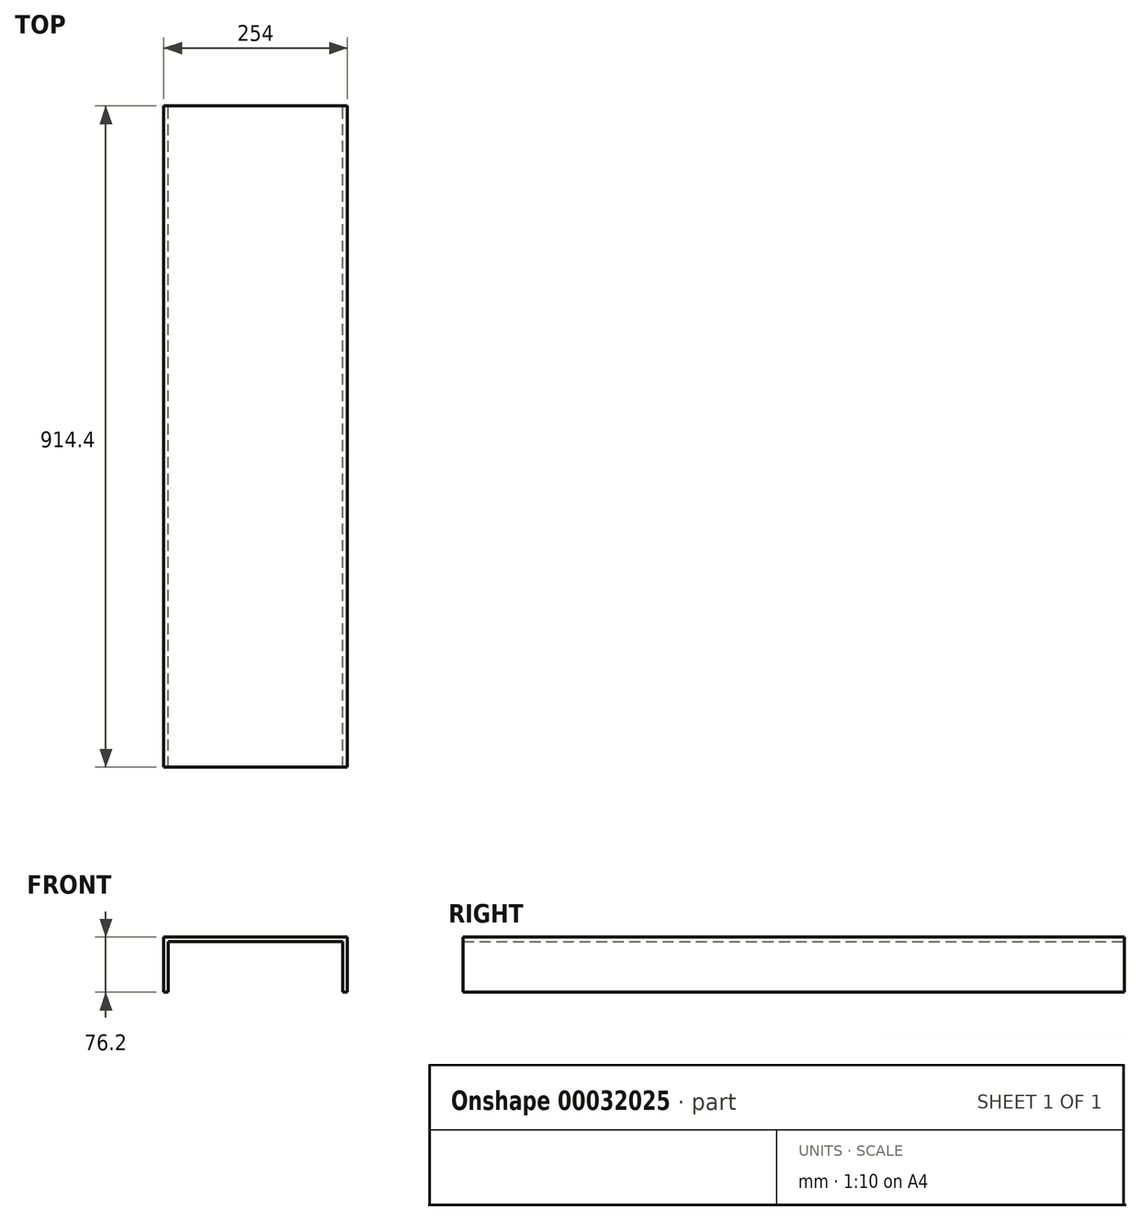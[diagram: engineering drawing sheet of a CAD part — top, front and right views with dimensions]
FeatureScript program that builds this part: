
annotation { "Feature Type Name" : "Feature", "Feature Type Description" : "" }
export const myFeature = defineFeature(function(context is Context, id is Id, definition is map)
    precondition{}
    {
        {
            var Q0;
            Q0=qCreatedBy(makeId("Front.planeOp"),FACE);
            var sketch = newSketch(context, id + "F0", { "sketchPlane" : qUnion([Q0])});
            skLineSegment(sketch, "E0.bottom", {"start": v(0, 0) * mm, "end": v(6.35, 0) * mm});
            skLineSegment(sketch, "E0.top", {"start": v(0, 76.2) * mm, "end": v(254, 76.2) * mm});
            skLineSegment(sketch, "E0.left", {"start": v(0, 0) * mm, "end": v(0, 76.2) * mm});
            skLineSegment(sketch, "E0.right", {"start": v(254, 0) * mm, "end": v(254, 76.2) * mm});
            skLineSegment(sketch, "E1.top", {"start": v(6.35, 69.85) * mm, "end": v(247.65, 69.85) * mm});
            skLineSegment(sketch, "E1.left", {"start": v(6.35, 0) * mm, "end": v(6.35, 69.85) * mm});
            skLineSegment(sketch, "E1.right", {"start": v(247.65, 0) * mm, "end": v(247.65, 69.85) * mm});
            skLineSegment(sketch, "E2.trimOffspring", {"start": v(247.65, 0) * mm, "end": v(254, 0) * mm});
            skSolve(sketch);
        }
        {
            var Q0;
            Q0=makeQuery(id+"F0.imprint","IMPRINT",FACE,{"disambiguationData":[TD([[makeQuery(id+"F0.imprint","IMPRINT",EDGE,{"derivedFrom":sQuery(id+"F0.wireOp",EDGE,"E0.bottom")}),1.0]])]});
            extrude(context, id + "F1", {"entities" : qUnion([Q0]), "depth" : 914.4 * mm});
        }
    });
